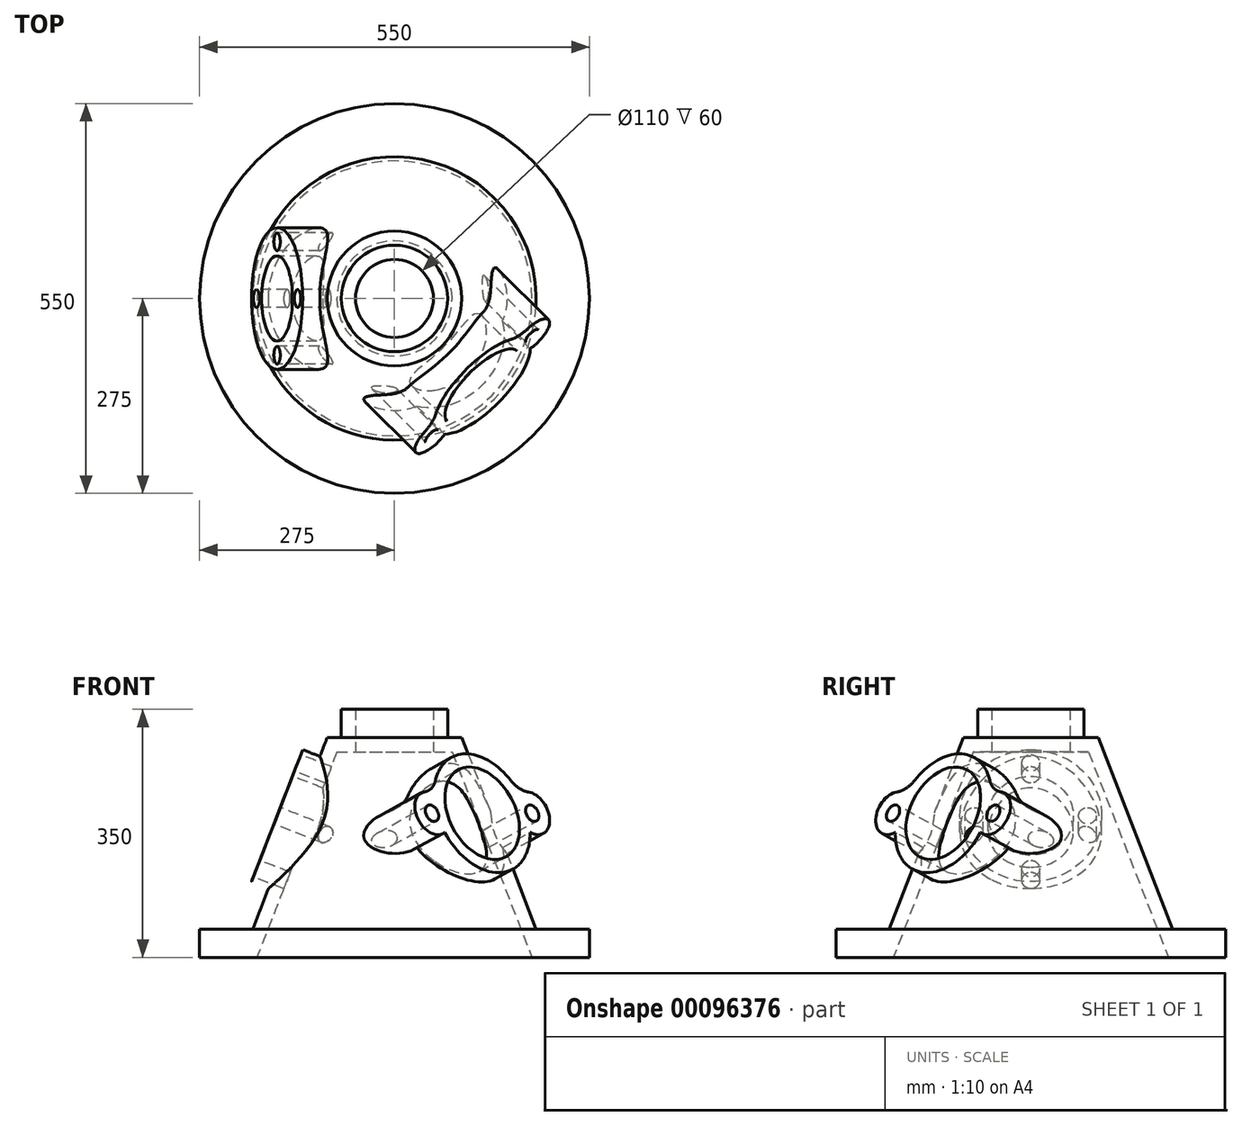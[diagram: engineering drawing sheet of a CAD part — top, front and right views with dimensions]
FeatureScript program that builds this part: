
annotation { "Feature Type Name" : "Feature", "Feature Type Description" : "" }
export const myFeature = defineFeature(function(context is Context, id is Id, definition is map)
    precondition{}
    {
        {
            var Q0;
            Q0=qCreatedBy(makeId("Front.planeOp"),FACE);
            var sketch = newSketch(context, id + "F0", { "sketchPlane" : qUnion([Q0])});
            skLineSegment(sketch, "E0", {"start": v(0, 0) * mm, "end": v(-194.1, 0) * mm, "construction": true});
            skLineSegment(sketch, "E1", {"start": v(0, 0) * mm, "end": v(0, 445.5) * mm, "construction": true});
            skLineSegment(sketch, "E2", {"start": v(-194.1, 0) * mm, "end": v(-275, 0) * mm});
            skLineSegment(sketch, "E3", {"start": v(-275, 0) * mm, "end": v(-275, 40) * mm});
            skLineSegment(sketch, "E4", {"start": v(-275, 40) * mm, "end": v(-200, 40) * mm});
            skLineSegment(sketch, "E5", {"start": v(-200, 40) * mm, "end": v(-95, 310) * mm});
            skLineSegment(sketch, "E6", {"start": v(-95, 310) * mm, "end": v(-75, 310) * mm});
            skLineSegment(sketch, "E7", {"start": v(-75, 310) * mm, "end": v(-75, 350) * mm});
            skLineSegment(sketch, "E8", {"start": v(-75, 350) * mm, "end": v(-55, 350) * mm});
            skLineSegment(sketch, "E9", {"start": v(-55, 350) * mm, "end": v(-55, 290) * mm});
            skLineSegment(sketch, "E10", {"start": v(-55, 290) * mm, "end": v(-81.32, 290) * mm});
            skLineSegment(sketch, "E11", {"start": v(-194.1, 0) * mm, "end": v(-81.32, 290) * mm});
            skSolve(sketch);
        }
        {
            var Q0;
            Q0=makeQuery(id+"F0.imprint","IMPRINT",FACE,{"disambiguationData":[TD([[makeQuery(id+"F0.imprint","IMPRINT",EDGE,{"derivedFrom":sQuery(id+"F0.wireOp",EDGE,"E2")}),-1.0]])]});
            var Q1;
            Q1=sQuery(id+"F0.wireOp",EDGE,"E1");
            revolve(context, id + "F1", {"entities" : qUnion([Q0]), "axis" : qUnion([Q1]), "revolveType" : RevolveType.FULL});
        }
        {
            var Q0;
            Q0=qCreatedBy(makeId("Front.planeOp"),FACE);
            var sketch = newSketch(context, id + "F2", { "sketchPlane" : qUnion([Q0])});
            skLineSegment(sketch, "E12.0", {"start": v(-200, 40) * mm, "end": v(-95, 310) * mm, "construction": true});
            skLineSegment(sketch, "E13.0", {"start": v(-75, 350) * mm, "end": v(-55, 350) * mm, "construction": true});
            skLineSegment(sketch, "E14", {"start": v(-75, 350) * mm, "end": v(0, 350) * mm, "construction": true});
            skLineSegment(sketch, "E15", {"start": v(0, 350) * mm, "end": v(-72.49, 163.6) * mm, "construction": true});
            skLineSegment(sketch, "E16", {"start": v(-95, 310) * mm, "end": v(-200, 40) * mm});
            skLineSegment(sketch, "E17", {"start": v(-72.49, 163.6) * mm, "end": v(-165.69, 199.84) * mm, "construction": true});
            skSolve(sketch);
        }
        {
            var Q0;
            Q0=sQuery(id+"F2.wireOp",EDGE,"E17");
            var Q1;
            Q1=sQuery(id+"F2.wireOp",VERTEX,"E17.end");
            cPlane(context, id + "F3", {"entities" : qUnion([Q0, Q1]), "cplaneType" : CPlaneType.LINE_POINT, "offset" : 150 * mm, "width" : 150 * mm, "height" : 150 * mm});
        }
        {
            var Q0;
            Q0=qCreatedBy(id+"F3.planeOp",FACE);
            var sketch = newSketch(context, id + "F4", { "sketchPlane" : qUnion([Q0])});
            skPoint(sketch, "E18.0", {"position": v(0, 126.2) * mm});
            skCircle(sketch, "E19", {"center": v(0, 126.2) * mm, "radius": 60 * mm});
            skCircle(sketch, "E20", {"center": v(0, 126.2) * mm, "radius": 100 * mm});
            skSolve(sketch);
        }
        {
            var Q0;
            Q0=makeQuery(id+"F4.imprint","IMPRINT",FACE,{"disambiguationData":[TD([[makeQuery(id+"F4.imprint","IMPRINT",EDGE,{"derivedFrom":sQuery(id+"F4.wireOp",EDGE,"E19")}),-1.0]])]});
            var Q1;
            Q1=makeQuery(id+"F4.imprint","IMPRINT",FACE,{"disambiguationData":[TD([[makeQuery(id+"F4.imprint","IMPRINT",EDGE,{"derivedFrom":sQuery(id+"F4.wireOp",EDGE,"E19")}),1.0]])]});
            var Q2;
            Q2=makeQuery(id+"F1.opRevolve","SWEPT_FACE",FACE,{"disambiguationData":[OSD([sQuery(id+"F0.wireOp",EDGE,"E5")])]});
            extrude(context, id + "F5", {"entities" : qUnion([Q0, Q1]), "operationType" : NewBodyOperationType.ADD, "endBound" : BoundingType.UP_TO_SURFACE, "oppositeDirection" : true, "endBoundEntityFace" : qUnion([Q2]), "depth" : 25 * mm});
        }
        {
            var Q0;
            Q0=makeQuery(id+"F4.imprint","IMPRINT",FACE,{"disambiguationData":[TD([[makeQuery(id+"F4.imprint","IMPRINT",EDGE,{"derivedFrom":sQuery(id+"F4.wireOp",EDGE,"E19")}),1.0]])]});
            var Q1;
            Q1=makeQuery(id+"F1.opRevolve","SWEPT_FACE",FACE,{"disambiguationData":[OSD([sQuery(id+"F0.wireOp",EDGE,"E11")])]});
            extrude(context, id + "F6", {"entities" : qUnion([Q0]), "operationType" : NewBodyOperationType.REMOVE, "endBound" : BoundingType.UP_TO_SURFACE, "oppositeDirection" : true, "endBoundEntityFace" : qUnion([Q1]), "depth" : 25 * mm});
        }
        {
            var Q0;
            Q0=makeQuery(id+"F5.opExtrude","CAP_FACE",FACE,{"disambiguationData":[OSD([sQuery(id+"F4.wireOp",EDGE,"E20")])],"isStart":true});
            var sketch = newSketch(context, id + "F7", { "sketchPlane" : qUnion([Q0])});
            skPoint(sketch, "E21.0", {"position": v(0, 126.2) * mm});
            skLineSegment(sketch, "E22", {"start": v(0, 126.2) * mm, "end": v(0, 206.2) * mm, "construction": true});
            skCircle(sketch, "E23", {"center": v(0, 206.2) * mm, "radius": 12.5 * mm});
            skCircle(sketch, "E24.1.0", {"center": v(80, 126.2) * mm, "radius": 12.5 * mm});
            skCircle(sketch, "E24.2.0", {"center": v(0, 46.2) * mm, "radius": 12.5 * mm});
            skCircle(sketch, "E24.3.0", {"center": v(-80, 126.2) * mm, "radius": 12.5 * mm});
            skLineSegment(sketch, "E24.anchor2", {"start": v(0, 126.2) * mm, "end": v(-80, 126.2) * mm, "construction": true});
            skSolve(sketch);
        }
        {
            var Q0;
            Q0=makeQuery(id+"F7.imprint","IMPRINT",FACE,{"disambiguationData":[TD([[makeQuery(id+"F7.imprint","IMPRINT",EDGE,{"derivedFrom":sQuery(id+"F7.wireOp",EDGE,"E23")}),1.0]])]});
            var Q1;
            Q1=makeQuery(id+"F7.imprint","IMPRINT",FACE,{"disambiguationData":[TD([[makeQuery(id+"F7.imprint","IMPRINT",EDGE,{"derivedFrom":sQuery(id+"F7.wireOp",EDGE,"E24.1.0")}),1.0]])]});
            var Q2;
            Q2=makeQuery(id+"F7.imprint","IMPRINT",FACE,{"disambiguationData":[TD([[makeQuery(id+"F7.imprint","IMPRINT",EDGE,{"derivedFrom":sQuery(id+"F7.wireOp",EDGE,"E24.2.0")}),1.0]])]});
            var Q3;
            Q3=makeQuery(id+"F7.imprint","IMPRINT",FACE,{"disambiguationData":[TD([[makeQuery(id+"F7.imprint","IMPRINT",EDGE,{"derivedFrom":sQuery(id+"F7.wireOp",EDGE,"E24.3.0")}),1.0]])]});
            extrude(context, id + "F8", {"entities" : qUnion([Q0, Q1, Q2, Q3]), "operationType" : NewBodyOperationType.REMOVE, "oppositeDirection" : true, "depth" : 108 * mm});
        }
        {
            var Q0;
            Q0=sQuery(id+"F0.wireOp",EDGE,"E1");
            cPlane(context, id + "F9", {"entities" : qUnion([Q0]), "cplaneType" : CPlaneType.LINE_ANGLE, "offset" : 150 * mm, "angle" : 45 * degree, "width" : 150 * mm, "height" : 150 * mm});
        }
        {
            var Q0;
            Q0=qCreatedBy(id+"F9.planeOp",FACE);
            var sketch = newSketch(context, id + "F10", { "sketchPlane" : qUnion([Q0])});
            skPoint(sketch, "E25.0", {"position": v(38.9, 350) * mm});
            skLineSegment(sketch, "E26", {"start": v(38.9, 350) * mm, "end": v(0, 350) * mm, "construction": true});
            skLineSegment(sketch, "E27", {"start": v(0, 350) * mm, "end": v(-72.49, 163.6) * mm, "construction": true});
            skLineSegment(sketch, "E28", {"start": v(-72.49, 163.6) * mm, "end": v(-175, 203.47) * mm, "construction": true});
            skSolve(sketch);
        }
        {
            var Q0;
            Q0=sQuery(id+"F10.wireOp",EDGE,"E28");
            var Q1;
            Q1=sQuery(id+"F10.wireOp",VERTEX,"E28.end");
            cPlane(context, id + "F11", {"entities" : qUnion([Q0, Q1]), "cplaneType" : CPlaneType.LINE_POINT, "offset" : 150 * mm, "width" : 150 * mm, "height" : 150 * mm});
        }
        {
            var Q0;
            Q0=qCreatedBy(id+"F11.planeOp",FACE);
            var sketch = newSketch(context, id + "F12", { "sketchPlane" : qUnion([Q0])});
            skPoint(sketch, "E29.0", {"position": v(-43, 118.65) * mm});
            skCircle(sketch, "E30", {"center": v(-43, 118.65) * mm, "radius": 70 * mm});
            skCircle(sketch, "E31", {"center": v(-43, 118.65) * mm, "radius": 90 * mm});
            skSolve(sketch);
        }
        {
            var Q0;
            Q0 = qSketchRegion(id + "F12", true);
            var Q1;
            Q1=makeQuery(id+"F12.imprint","IMPRINT",FACE,{"disambiguationData":[TD([[makeQuery(id+"F12.imprint","IMPRINT",EDGE,{"derivedFrom":sQuery(id+"F12.wireOp",EDGE,"E30")}),1.0]])]});
            extrude(context, id + "F13", {"entities" : qUnion([Q0, Q1]), "operationType" : NewBodyOperationType.ADD, "endBound" : BoundingType.UP_TO_NEXT, "oppositeDirection" : true, "depth" : 25 * mm});
        }
        {
            var Q0;
            Q0=makeQuery(id+"F12.imprint","IMPRINT",FACE,{"disambiguationData":[TD([[makeQuery(id+"F12.imprint","IMPRINT",EDGE,{"derivedFrom":sQuery(id+"F12.wireOp",EDGE,"E30")}),1.0]])]});
            extrude(context, id + "F14", {"entities" : qUnion([Q0]), "operationType" : NewBodyOperationType.REMOVE, "oppositeDirection" : true, "depth" : 173.02 * mm});
        }
        {
            var Q0;
            Q0=makeQuery(id+"F12.imprint","IMPRINT",FACE,{"disambiguationData":[TD([[makeQuery(id+"F12.imprint","IMPRINT",EDGE,{"derivedFrom":sQuery(id+"F12.wireOp",EDGE,"E30")}),-1.0]])]});
            var sketch = newSketch(context, id + "F15", { "sketchPlane" : qUnion([Q0])});
            skArc(sketch, "E32.0", {"start": v(-132.99, 116.82) * mm, "mid": v(-127.62, 87.98) * mm, "end": v(-113.26, 62.4) * mm});
            skPoint(sketch, "E33", {"position": v(30.43, -87.01) * mm});
            skPoint(sketch, "E34", {"position": v(0, 0) * mm});
            skLineSegment(sketch, "E35", {"start": v(0, 0) * mm, "end": v(-43, 118.65) * mm, "construction": true});
            skLineSegment(sketch, "E36", {"start": v(-43, 118.65) * mm, "end": v(51.01, 152.72) * mm, "construction": true});
            skLineSegment(sketch, "E37", {"start": v(-43, 118.65) * mm, "end": v(-137.02, 84.57) * mm, "construction": true});
            skArc(sketch, "E38", {"start": v(46.98, 120.48) * mm, "mid": v(81.57, 163.8) * mm, "end": v(27.25, 174.9) * mm});
            skArc(sketch, "E39", {"start": v(-111.63, 104.87) * mm, "mid": v(-167.57, 73.5) * mm, "end": v(-104.53, 85.26) * mm});
            skCircle(sketch, "E40", {"center": v(-137.02, 84.57) * mm, "radius": 12.5 * mm});
            skCircle(sketch, "E41", {"center": v(51.01, 152.72) * mm, "radius": 12.5 * mm});
            skCircle(sketch, "E42.0", {"center": v(-43, 118.65) * mm, "radius": 70 * mm});
            skArc(sketch, "E43.trimOffspring", {"start": v(46.98, 120.48) * mm, "mid": v(41.6, 149.32) * mm, "end": v(27.25, 174.9) * mm});
            skSolve(sketch);
        }
        {
            var Q0;
            {var subQ1=sQuery(id+"F15.wireOp",EDGE,"E32.0");var subQ4=sQuery(id+"F15.wireOp",EDGE,"E40");var subQ5=makeQuery(id+"F15.imprint","INTERSECT",VERTEX,{"disambiguationData":[OD(0.0)],"derivedFrom":[subQ1,subQ4]});Q0=makeQuery(id+"F15.imprint","IMPRINT",FACE,{"disambiguationData":[TD([[makeQuery(id+"F15.imprint","IMPRINT",EDGE,{"disambiguationData":[TD([[subQ5,-1.0]])],"derivedFrom":subQ4}),-1.0]])]});}
            var Q1;
            {var subQ0=sQuery(id+"F15.wireOp",EDGE,"E40");var subQ1=sQuery(id+"F15.wireOp",EDGE,"E32.0");var subQ2=makeQuery(id+"F15.imprint","INTERSECT",VERTEX,{"disambiguationData":[OD(0.0)],"derivedFrom":[subQ1,subQ0]});Q1=makeQuery(id+"F15.imprint","IMPRINT",FACE,{"disambiguationData":[TD([[makeQuery(id+"F15.imprint","IMPRINT",EDGE,{"disambiguationData":[TD([[subQ2,-1.0]])],"derivedFrom":subQ1}),-1.0]])]});}
            var Q2;
            {var subQ0=sQuery(id+"F15.wireOp",EDGE,"E38");Q2=makeQuery(id+"F15.imprint","IMPRINT",FACE,{"disambiguationData":[TD([[makeQuery(id+"F15.imprint","IMPRINT",EDGE,{"derivedFrom":subQ0}),1.0]])]});}
            var Q3;
            {var subQ0=sQuery(id+"F15.wireOp",EDGE,"E43.trimOffspring");var subQ1=sQuery(id+"F15.wireOp",EDGE,"E41");var subQ2=makeQuery(id+"F15.imprint","INTERSECT",VERTEX,{"disambiguationData":[OD(0.0)],"derivedFrom":[subQ1,subQ0]});Q3=makeQuery(id+"F15.imprint","IMPRINT",FACE,{"disambiguationData":[TD([[makeQuery(id+"F15.imprint","IMPRINT",EDGE,{"disambiguationData":[TD([[subQ2,-1.0]])],"derivedFrom":subQ1}),1.0]])]});}
            extrude(context, id + "F16", {"entities" : qUnion([Q0, Q1, Q2, Q3]), "operationType" : NewBodyOperationType.ADD, "endBound" : BoundingType.UP_TO_NEXT, "oppositeDirection" : true, "depth" : 25 * mm});
        }
        {
            var Q0;
            {var subQ0=sQuery(id+"F15.wireOp",EDGE,"E40");var subQ1=sQuery(id+"F15.wireOp",EDGE,"E32.0");var subQ2=makeQuery(id+"F15.imprint","INTERSECT",VERTEX,{"disambiguationData":[OD(0.0)],"derivedFrom":[subQ1,subQ0]});Q0=makeQuery(id+"F15.imprint","IMPRINT",FACE,{"disambiguationData":[TD([[makeQuery(id+"F15.imprint","IMPRINT",EDGE,{"disambiguationData":[TD([[subQ2,-1.0]])],"derivedFrom":subQ1}),-1.0]])]});}
            var Q1;
            {var subQ0=sQuery(id+"F15.wireOp",EDGE,"E43.trimOffspring");var subQ1=sQuery(id+"F15.wireOp",EDGE,"E41");var subQ2=makeQuery(id+"F15.imprint","INTERSECT",VERTEX,{"disambiguationData":[OD(0.0)],"derivedFrom":[subQ1,subQ0]});Q1=makeQuery(id+"F15.imprint","IMPRINT",FACE,{"disambiguationData":[TD([[makeQuery(id+"F15.imprint","IMPRINT",EDGE,{"disambiguationData":[TD([[subQ2,-1.0]])],"derivedFrom":subQ1}),1.0]])]});}
            var Q2;
            {var subQ0=sQuery(id+"F15.wireOp",EDGE,"E43.trimOffspring");var subQ1=sQuery(id+"F15.wireOp",EDGE,"E41");var subQ2=makeQuery(id+"F15.imprint","INTERSECT",VERTEX,{"disambiguationData":[OD(0.0)],"derivedFrom":[subQ1,subQ0]});Q2=makeQuery(id+"F15.imprint","IMPRINT",FACE,{"disambiguationData":[TD([[makeQuery(id+"F15.imprint","IMPRINT",EDGE,{"disambiguationData":[TD([[subQ2,1.0]])],"derivedFrom":subQ1}),1.0]])]});}
            var Q3;
            {var subQ0=sQuery(id+"F15.wireOp",EDGE,"E40");var subQ1=sQuery(id+"F15.wireOp",EDGE,"E32.0");var subQ2=makeQuery(id+"F15.imprint","INTERSECT",VERTEX,{"disambiguationData":[OD(0.0)],"derivedFrom":[subQ1,subQ0]});Q3=makeQuery(id+"F15.imprint","IMPRINT",FACE,{"disambiguationData":[TD([[makeQuery(id+"F15.imprint","IMPRINT",EDGE,{"disambiguationData":[TD([[subQ2,-1.0]])],"derivedFrom":subQ1}),1.0]])]});}
            extrude(context, id + "F17", {"entities" : qUnion([Q0, Q1, Q2, Q3]), "operationType" : NewBodyOperationType.REMOVE, "oppositeDirection" : true, "depth" : 127.27 * mm});
        }
        {
            var Q0;
            {var subQ0=sQuery(id+"F15.wireOp",EDGE,"E39");var subQ1=sQuery(id+"F15.wireOp",EDGE,"E32.0");var subQ2=sQuery(id+"F12.wireOp",EDGE,"E31");Q0=makeQuery(id+"F16.opExtrude","SWEPT_EDGE",EDGE,{"disambiguationData":[OSD([subQ2,subQ1,subQ0]),TDD([makeQuery(id+"F15.imprint","INTERSECT",VERTEX,{"disambiguationData":[OD(0.0)],"derivedFrom":[makeQuery(id+"F12.imprint","IMPRINT",EDGE,{"derivedFrom":subQ2}),subQ1,subQ0]})])]});}
            var Q1;
            {var subQ0=sQuery(id+"F15.wireOp",EDGE,"E43.trimOffspring");var subQ1=sQuery(id+"F15.wireOp",EDGE,"E38");var subQ2=sQuery(id+"F12.wireOp",EDGE,"E31");Q1=makeQuery(id+"F16.opExtrude","SWEPT_EDGE",EDGE,{"disambiguationData":[OSD([subQ2,subQ1,subQ0]),TDD([makeQuery(id+"F15.imprint","INTERSECT",VERTEX,{"disambiguationData":[OD(1.0)],"derivedFrom":[makeQuery(id+"F12.imprint","IMPRINT",EDGE,{"derivedFrom":subQ2}),subQ1,subQ0]})])]});}
            var Q2;
            {var subQ0=sQuery(id+"F15.wireOp",EDGE,"E43.trimOffspring");var subQ1=sQuery(id+"F15.wireOp",EDGE,"E38");var subQ2=sQuery(id+"F12.wireOp",EDGE,"E31");Q2=makeQuery(id+"F16.opExtrude","SWEPT_EDGE",EDGE,{"disambiguationData":[OSD([subQ2,subQ1,subQ0]),TDD([makeQuery(id+"F15.imprint","INTERSECT",VERTEX,{"disambiguationData":[OD(0.0)],"derivedFrom":[makeQuery(id+"F12.imprint","IMPRINT",EDGE,{"derivedFrom":subQ2}),subQ1,subQ0]})])]});}
            var Q3;
            {var subQ0=sQuery(id+"F15.wireOp",EDGE,"E39");var subQ1=sQuery(id+"F15.wireOp",EDGE,"E32.0");var subQ2=sQuery(id+"F12.wireOp",EDGE,"E31");Q3=makeQuery(id+"F16.opExtrude","SWEPT_EDGE",EDGE,{"disambiguationData":[OSD([subQ2,subQ1,subQ0]),TDD([makeQuery(id+"F15.imprint","INTERSECT",VERTEX,{"disambiguationData":[OD(1.0)],"derivedFrom":[makeQuery(id+"F12.imprint","IMPRINT",EDGE,{"derivedFrom":subQ2}),subQ1,subQ0]})])]});}
            fillet(context, id + "F18", {"entities" : qUnion([Q0, Q1, Q2, Q3]), "radius" : 40 * mm, "tangentPropagation" : true, "allowEdgeOverflow" : false});
        }
    });
